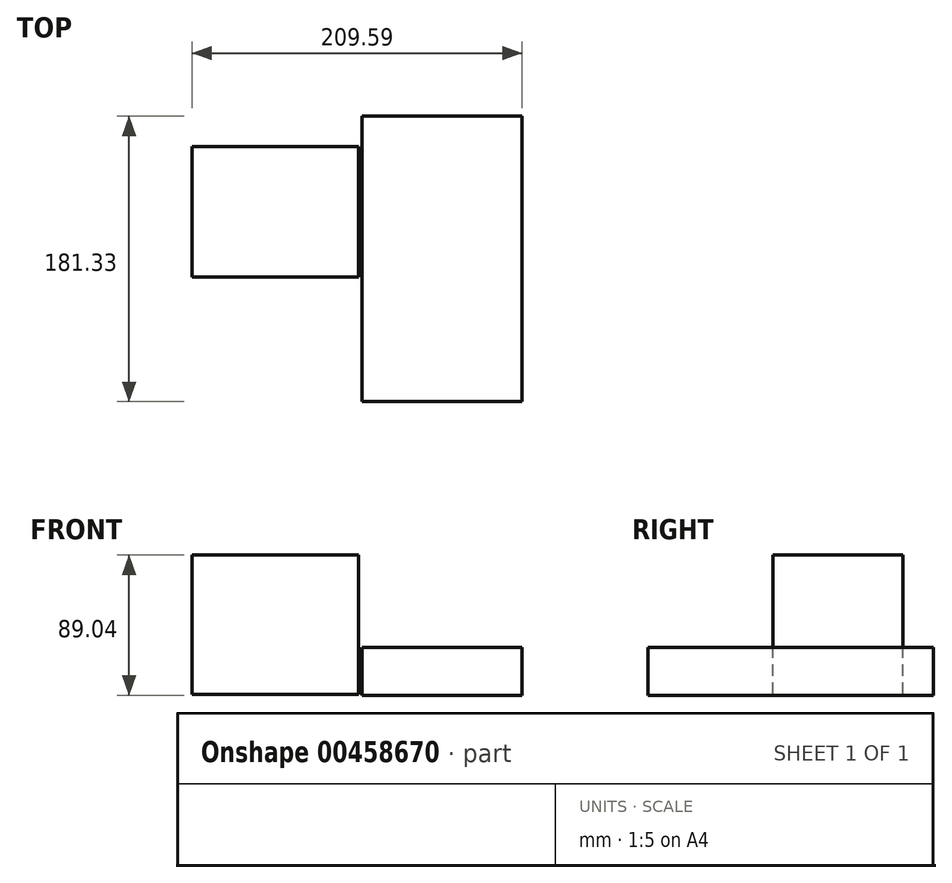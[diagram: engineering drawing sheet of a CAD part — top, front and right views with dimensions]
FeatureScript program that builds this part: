
annotation { "Feature Type Name" : "Feature", "Feature Type Description" : "" }
export const myFeature = defineFeature(function(context is Context, id is Id, definition is map)
    precondition{}
    {
        {
            var Q0;
            Q0=qCreatedBy(makeId("Right.planeOp"),FACE);
            var sketch = newSketch(context, id + "F0", { "sketchPlane" : qUnion([Q0])});
            skLineSegment(sketch, "E0.bottom", {"start": v(-79.28, 21.71) * mm, "end": v(19.24, 21.71) * mm});
            skLineSegment(sketch, "E0.top", {"start": v(-79.28, -8.6) * mm, "end": v(19.24, -8.6) * mm});
            skLineSegment(sketch, "E0.left", {"start": v(-79.28, 21.71) * mm, "end": v(-79.28, -8.6) * mm});
            skLineSegment(sketch, "E0.right", {"start": v(19.24, 21.71) * mm, "end": v(19.24, -8.6) * mm});
            skSolve(sketch);
        }
        {
            var Q0;
            Q0=makeQuery(id+"F0.imprint","IMPRINT",FACE,{"disambiguationData":[TD([[makeQuery(id+"F0.imprint","IMPRINT",EDGE,{"derivedFrom":sQuery(id+"F0.wireOp",EDGE,"E0.bottom")}),-1.0]])]});
            extrude(context, id + "F1", {"entities" : qUnion([Q0]), "depth" : 101.6 * mm});
        }
        {
            var Q0;
            Q0=qCreatedBy(makeId("Front.planeOp"),FACE);
            var sketch = newSketch(context, id + "F2", { "sketchPlane" : qUnion([Q0])});
            skLineSegment(sketch, "E1.bottom", {"start": v(-2.13, -7.88) * mm, "end": v(-108, -7.88) * mm});
            skLineSegment(sketch, "E1.top", {"start": v(-2.13, 80.44) * mm, "end": v(-108, 80.44) * mm});
            skLineSegment(sketch, "E1.left", {"start": v(-2.13, -7.88) * mm, "end": v(-2.13, 80.44) * mm});
            skLineSegment(sketch, "E1.right", {"start": v(-108, -7.88) * mm, "end": v(-108, 80.44) * mm});
            skLineSegment(sketch, "E2.bottom", {"start": v(-2.13, -7.88) * mm, "end": v(0, -7.88) * mm});
            skLineSegment(sketch, "E2.top", {"start": v(-2.13, -10.26) * mm, "end": v(0, -10.26) * mm});
            skLineSegment(sketch, "E2.left", {"start": v(-2.13, -7.88) * mm, "end": v(-2.13, -10.26) * mm});
            skLineSegment(sketch, "E2.right", {"start": v(0, -7.88) * mm, "end": v(0, -10.26) * mm});
            skLineSegment(sketch, "E3.bottom", {"start": v(0, -7.88) * mm, "end": v(-2.13, -7.88) * mm});
            skLineSegment(sketch, "E3.top", {"start": v(0, 23.34) * mm, "end": v(-2.13, 23.34) * mm});
            skLineSegment(sketch, "E3.left", {"start": v(0, -7.88) * mm, "end": v(0, 23.34) * mm});
            skLineSegment(sketch, "E3.right", {"start": v(-2.13, -7.88) * mm, "end": v(-2.13, 23.34) * mm});
            skSolve(sketch);
        }
        {
            var Q0;
            Q0=makeQuery(id+"F2.imprint","IMPRINT",FACE,{"disambiguationData":[TD([[makeQuery(id+"F2.imprint","IMPRINT",EDGE,{"derivedFrom":sQuery(id+"F2.wireOp",EDGE,"E1.bottom")}),-1.0]])]});
            var Q1;
            Q1=makeQuery(id+"F2.imprint","IMPRINT",FACE,{"disambiguationData":[TD([[makeQuery(id+"F2.imprint","IMPRINT",EDGE,{"derivedFrom":sQuery(id+"F2.wireOp",EDGE,"E3.bottom")}),-1.0]])]});
            var Q2;
            Q2=makeQuery(id+"F1.opExtrude","SWEPT_FACE",FACE,{"disambiguationData":[OSD([sQuery(id+"F0.wireOp",EDGE,"E0.left")])]});
            extrude(context, id + "F3", {"entities" : qUnion([Q0, Q1, Q2]), "operationType" : NewBodyOperationType.ADD, "depth" : 82.8 * mm});
        }
    });
